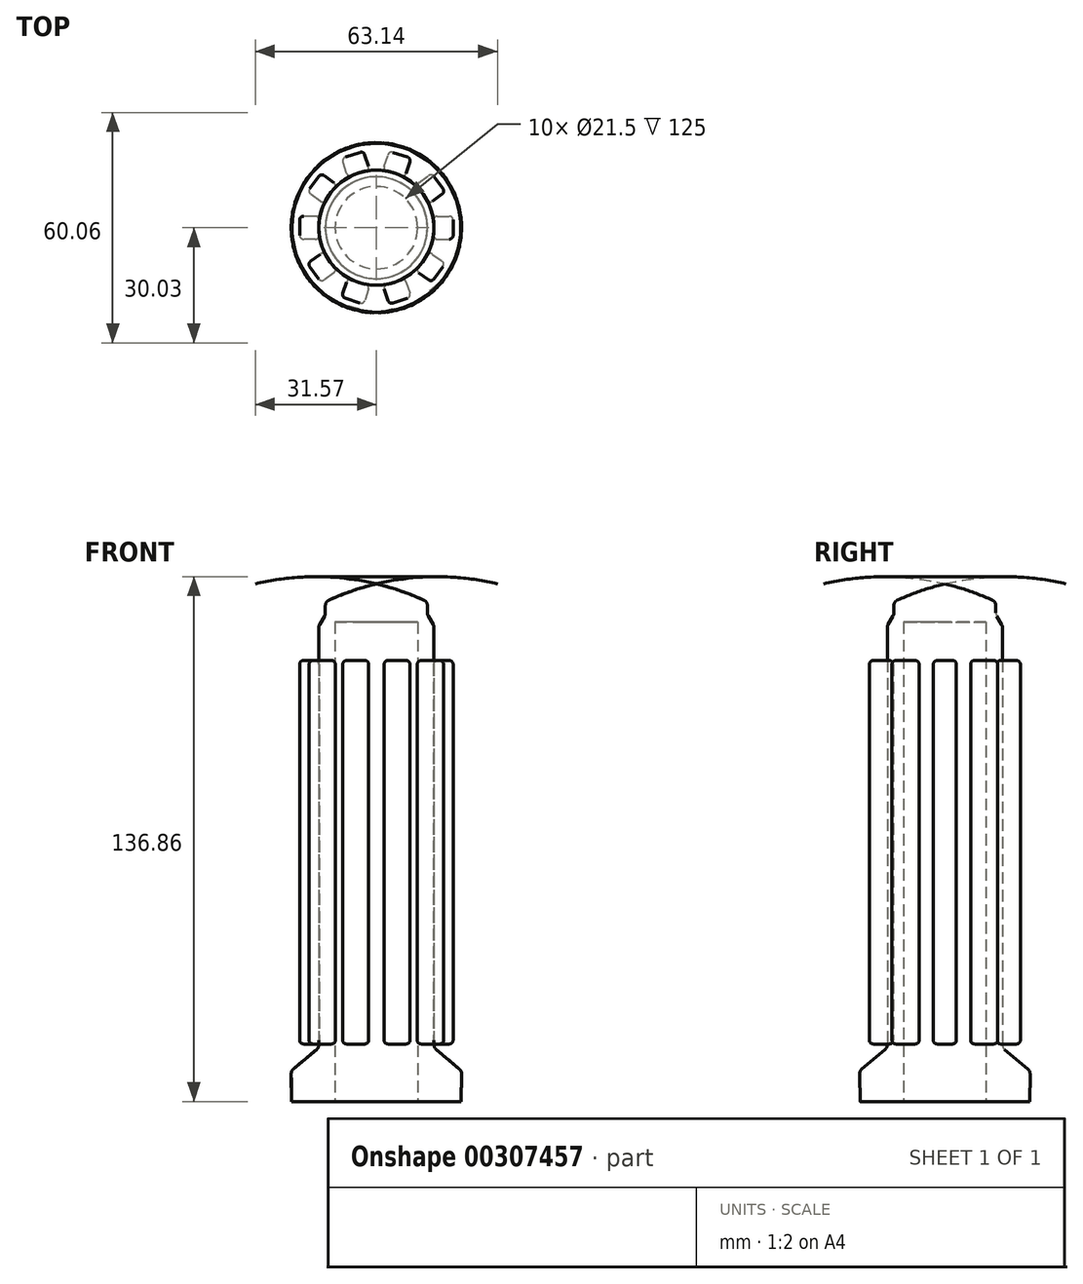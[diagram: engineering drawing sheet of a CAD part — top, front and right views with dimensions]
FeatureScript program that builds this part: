
annotation { "Feature Type Name" : "Feature", "Feature Type Description" : "" }
export const myFeature = defineFeature(function(context is Context, id is Id, definition is map)
    precondition{}
    {
        {
            var Q0;
            Q0=qCreatedBy(makeId("Front.planeOp"),FACE);
            var sketch = newSketch(context, id + "F0", { "sketchPlane" : qUnion([Q0])});
            skLineSegment(sketch, "E0", {"start": v(0, 135) * mm, "end": v(0, 125) * mm});
            skLineSegment(sketch, "E1", {"start": v(10.75, 125) * mm, "end": v(10.75, 0) * mm});
            skLineSegment(sketch, "E2", {"start": v(15, 124.05) * mm, "end": v(15, 14.05) * mm});
            skPoint(sketch, "E2.startSnap0", {"position": v(0, 135) * mm});
            skLineSegment(sketch, "E3", {"start": v(15, 14.05) * mm, "end": v(22.2, 8) * mm});
            skLineSegment(sketch, "E4", {"start": v(22.09, 0) * mm, "end": v(10.75, 0) * mm});
            skLineSegment(sketch, "E5", {"start": v(15, 124.05) * mm, "end": v(13.3, 127) * mm});
            skLineSegment(sketch, "E6", {"start": v(13.3, 127) * mm, "end": v(13.3, 130.33) * mm});
            skArc(sketch, "E7", {"start": v(13.3, 130.33) * mm, "mid": v(6.77, 133) * mm, "end": v(0, 135) * mm});
            skLineSegment(sketch, "E8", {"start": v(10.75, 125) * mm, "end": v(0, 125) * mm});
            skLineSegment(sketch, "E9", {"start": v(0, 0) * mm, "end": v(0, 70.9) * mm, "construction": true});
            skLineSegment(sketch, "E10", {"start": v(22.09, 0) * mm, "end": v(22.2, 8) * mm});
            skSolve(sketch);
        }
        {
            var Q0;
            Q0 = qSketchRegion(id + "F0", true);
            var Q1;
            Q1=sQuery(id+"F0.wireOp",EDGE,"E9");
            revolve(context, id + "F1", {"entities" : qUnion([Q0]), "axis" : qUnion([Q1]), "revolveType" : RevolveType.FULL});
        }
        {
            var Q0;
            Q0=makeQuery(id+"F1.opRevolve","SWEPT_EDGE",EDGE,{"disambiguationData":[OSD([sQuery(id+"F0.wireOp",EDGE,"E2"),sQuery(id+"F0.wireOp",EDGE,"E5")])]});
            var Q1;
            Q1=makeQuery(id+"F1.opRevolve","SWEPT_EDGE",EDGE,{"disambiguationData":[OSD([sQuery(id+"F0.wireOp",EDGE,"E5"),sQuery(id+"F0.wireOp",EDGE,"E6")])]});
            var Q2;
            Q2=makeQuery(id+"F1.opRevolve","SWEPT_EDGE",EDGE,{"disambiguationData":[OSD([sQuery(id+"F0.wireOp",EDGE,"E6"),sQuery(id+"F0.wireOp",EDGE,"E7")])]});
            var Q3;
            Q3=makeQuery(id+"F1.opRevolve","SWEPT_FACE",FACE,{"disambiguationData":[OSD([sQuery(id+"F0.wireOp",EDGE,"E7")])]});
            var Q4;
            Q4=makeQuery(id+"F1.opRevolve","SWEPT_EDGE",EDGE,{"disambiguationData":[OSD([sQuery(id+"F0.wireOp",EDGE,"E2"),sQuery(id+"F0.wireOp",EDGE,"E3")])]});
            var Q5;
            Q5=makeQuery(id+"F1.opRevolve","SWEPT_EDGE",EDGE,{"disambiguationData":[OSD([sQuery(id+"F0.wireOp",EDGE,"E3"),sQuery(id+"F0.wireOp",EDGE,"E10")])]});
            fillet(context, id + "F2", {"entities" : qUnion([Q0, Q1, Q2, Q3, Q4, Q5]), "radius" : 1.6 * mm, "tangentPropagation" : true, "allowEdgeOverflow" : false});
        }
        {
            var Q0;
            Q0=qCreatedBy(makeId("Right.planeOp"),FACE);
            cPlane(context, id + "F3", {"entities" : qUnion([Q0]), "cplaneType" : CPlaneType.OFFSET, "offset" : 20 * mm, "width" : 150 * mm, "height" : 150 * mm});
        }
        {
            var Q0;
            Q0=qCreatedBy(id+"F3.planeOp",FACE);
            var sketch = newSketch(context, id + "F4", { "sketchPlane" : qUnion([Q0])});
            skLineSegment(sketch, "E11.bottom", {"start": v(3, 15) * mm, "end": v(-3, 15) * mm});
            skLineSegment(sketch, "E11.top", {"start": v(3, 115) * mm, "end": v(-3, 115) * mm});
            skLineSegment(sketch, "E11.left", {"start": v(3, 15) * mm, "end": v(3, 115) * mm});
            skLineSegment(sketch, "E11.right", {"start": v(-3, 15) * mm, "end": v(-3, 115) * mm});
            skSolve(sketch);
        }
        {
            var Q0;
            Q0 = qSketchRegion(id + "F4", true);
            var Q1;
            Q1=makeQuery(id+"F1.opRevolve","SWEPT_FACE",FACE,{"disambiguationData":[OSD([sQuery(id+"F0.wireOp",EDGE,"E2")])]});
            extrude(context, id + "F5", {"entities" : qUnion([Q0]), "endBound" : BoundingType.UP_TO_SURFACE, "oppositeDirection" : true, "depth" : 25 * mm, "endBoundEntityFace" : qUnion([Q1]), "offsetDistance" : 25 * mm});
        }
        {
            var Q0;
            Q0=makeQuery(id+"F5.opExtrude","CAP_EDGE",EDGE,{"disambiguationData":[OSD([sQuery(id+"F4.wireOp",EDGE,"E11.right")])],"isStart":false});
            var Q1;
            Q1=makeQuery(id+"F5.opExtrude","CAP_EDGE",EDGE,{"disambiguationData":[OSD([sQuery(id+"F4.wireOp",EDGE,"E11.left")])],"isStart":true});
            var Q2;
            Q2=makeQuery(id+"F5.opExtrude","CAP_EDGE",EDGE,{"disambiguationData":[OSD([sQuery(id+"F4.wireOp",EDGE,"E11.right")])],"isStart":true});
            var Q3;
            Q3=makeQuery(id+"F5.opExtrude","CAP_EDGE",EDGE,{"disambiguationData":[OSD([sQuery(id+"F4.wireOp",EDGE,"E11.top")])],"isStart":true});
            var Q4;
            Q4=makeQuery(id+"F5.opExtrude","SWEPT_EDGE",EDGE,{"disambiguationData":[OSD([sQuery(id+"F4.wireOp",EDGE,"E11.top"),sQuery(id+"F4.wireOp",EDGE,"E11.left")])]});
            var Q5;
            Q5=makeQuery(id+"F5.opExtrude","CAP_EDGE",EDGE,{"disambiguationData":[OSD([sQuery(id+"F4.wireOp",EDGE,"E11.top")])],"isStart":false});
            var Q6;
            Q6=makeQuery(id+"F5.opExtrude","SWEPT_EDGE",EDGE,{"disambiguationData":[OSD([sQuery(id+"F4.wireOp",EDGE,"E11.bottom"),sQuery(id+"F4.wireOp",EDGE,"E11.right")])]});
            var Q7;
            Q7=makeQuery(id+"F5.opExtrude","CAP_EDGE",EDGE,{"disambiguationData":[OSD([sQuery(id+"F4.wireOp",EDGE,"E11.bottom")])],"isStart":true});
            var Q8;
            Q8=makeQuery(id+"F5.opExtrude","SWEPT_EDGE",EDGE,{"disambiguationData":[OSD([sQuery(id+"F4.wireOp",EDGE,"E11.top"),sQuery(id+"F4.wireOp",EDGE,"E11.right")])]});
            var Q9;
            Q9=makeQuery(id+"F5.opExtrude","SWEPT_EDGE",EDGE,{"disambiguationData":[OSD([sQuery(id+"F4.wireOp",EDGE,"E11.bottom"),sQuery(id+"F4.wireOp",EDGE,"E11.left")])]});
            var Q10;
            Q10=makeQuery(id+"F5.opExtrude","CAP_EDGE",EDGE,{"disambiguationData":[OSD([sQuery(id+"F4.wireOp",EDGE,"E11.left")])],"isStart":false});
            var Q11;
            Q11=makeQuery(id+"F5.opExtrude","SWEPT_FACE",FACE,{"disambiguationData":[OSD([sQuery(id+"F4.wireOp",EDGE,"E11.left")])]});
            var Q12;
            Q12=makeQuery(id+"F5.opExtrude","CAP_EDGE",EDGE,{"disambiguationData":[OSD([sQuery(id+"F4.wireOp",EDGE,"E11.bottom")])],"isStart":false});
            fillet(context, id + "F6", {"entities" : qUnion([Q0, Q1, Q2, Q3, Q4, Q5, Q6, Q7, Q8, Q9, Q10, Q11, Q12]), "radius" : 1 * mm, "tangentPropagation" : true, "allowEdgeOverflow" : false});
        }
        {
            var Q0;
            Q0=makeQuery(id+"F1.opRevolve","SWEPT_BODY",BODY,{"disambiguationData":[OSD([sQuery(id+"F0.wireOp",EDGE,"E0"),sQuery(id+"F0.wireOp",EDGE,"E1"),sQuery(id+"F0.wireOp",EDGE,"E2"),sQuery(id+"F0.wireOp",EDGE,"E3"),sQuery(id+"F0.wireOp",EDGE,"E4"),sQuery(id+"F0.wireOp",EDGE,"E5"),sQuery(id+"F0.wireOp",EDGE,"E6"),sQuery(id+"F0.wireOp",EDGE,"E7"),sQuery(id+"F0.wireOp",EDGE,"E8"),sQuery(id+"F0.wireOp",EDGE,"E10")])]});
            var Q1;
            Q1=makeQuery(id+"F5.opExtrude","SWEPT_BODY",BODY,{"disambiguationData":[OSD([sQuery(id+"F4.wireOp",EDGE,"E11.bottom"),sQuery(id+"F4.wireOp",EDGE,"E11.top"),sQuery(id+"F4.wireOp",EDGE,"E11.left"),sQuery(id+"F4.wireOp",EDGE,"E11.right")])]});
            var Q2;
            Q2=makeQuery(id+"F1.opRevolve","SWEPT_FACE",FACE,{"disambiguationData":[OSD([sQuery(id+"F0.wireOp",EDGE,"E2")])]});
            circularPattern(context, id + "F7", {"entities" : qUnion([Q0, Q1]), "axis" : qUnion([Q2]), "angle" : 360 * degree, "instanceCount" : 10, "equalSpace" : true});
        }
    });
